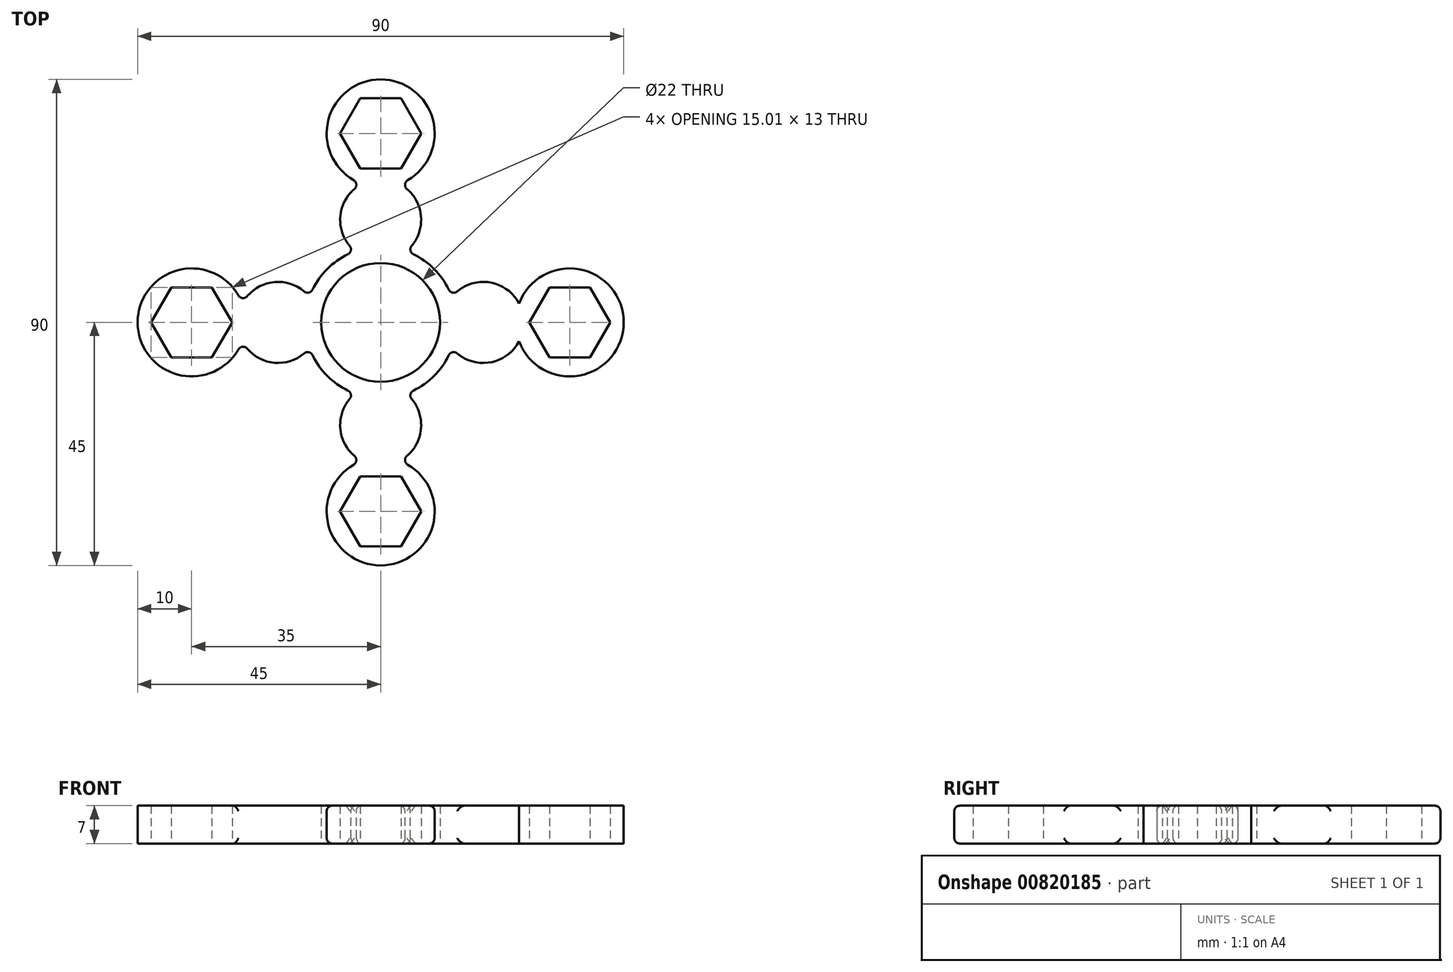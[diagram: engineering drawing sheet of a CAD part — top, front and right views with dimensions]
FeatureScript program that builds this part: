
annotation { "Feature Type Name" : "Feature", "Feature Type Description" : "" }
export const myFeature = defineFeature(function(context is Context, id is Id, definition is map)
    precondition{}
    {
        {
            var Q0;
            Q0=qCreatedBy(makeId("Top.planeOp"),FACE);
            var sketch = newSketch(context, id + "F0", { "sketchPlane" : qUnion([Q0])});
            skCircle(sketch, "E0", {"center": v(0, 0) * mm, "radius": 11 * mm});
            skCircle(sketch, "E1", {"center": v(0, 0) * mm, "radius": 14 * mm});
            skCircle(sketch, "E2", {"center": v(0, 19) * mm, "radius": 7.5 * mm});
            skCircle(sketch, "E3.MirrorC", {"center": v(0, -19) * mm, "radius": 7.5 * mm});
            skCircle(sketch, "E4", {"center": v(-19, 0) * mm, "radius": 7.5 * mm});
            skCircle(sketch, "E5.MirrorC", {"center": v(19, 0) * mm, "radius": 7.5 * mm});
            skCircle(sketch, "E6", {"center": v(-35, 0) * mm, "radius": 10 * mm});
            skCircle(sketch, "E7.MirrorC", {"center": v(35, 0) * mm, "radius": 10 * mm});
            skCircle(sketch, "E8", {"center": v(0, -35) * mm, "radius": 10 * mm});
            skCircle(sketch, "E9.MirrorC", {"center": v(0, 35) * mm, "radius": 10 * mm});
            skCircle(sketch, "E10.cCircle", {"center": v(0, 35) * mm, "radius": 6.5 * mm, "construction": true});
            skLineSegment(sketch, "E10.0", {"start": v(3.75, 28.5) * mm, "end": v(-3.75, 28.5) * mm});
            skLineSegment(sketch, "E10.1", {"start": v(-3.75, 28.5) * mm, "end": v(-7.5, 35) * mm});
            skLineSegment(sketch, "E10.2", {"start": v(-7.5, 35) * mm, "end": v(-3.75, 41.5) * mm});
            skLineSegment(sketch, "E10.3", {"start": v(-3.75, 41.5) * mm, "end": v(3.75, 41.5) * mm});
            skLineSegment(sketch, "E10.4", {"start": v(3.75, 41.5) * mm, "end": v(7.5, 35) * mm});
            skLineSegment(sketch, "E10.5", {"start": v(7.5, 35) * mm, "end": v(3.75, 28.5) * mm});
            skPoint(sketch, "E10.0.midPoint", {"position": v(0, 28.5) * mm});
            skLineSegment(sketch, "E11.MirrorCS", {"start": v(7.5, -35) * mm, "end": v(3.75, -28.5) * mm});
            skLineSegment(sketch, "E12.MirrorCS", {"start": v(3.75, -41.5) * mm, "end": v(7.5, -35) * mm});
            skLineSegment(sketch, "E13.MirrorCS", {"start": v(-3.75, -41.5) * mm, "end": v(3.75, -41.5) * mm});
            skLineSegment(sketch, "E14.MirrorCS", {"start": v(-7.5, -35) * mm, "end": v(-3.75, -41.5) * mm});
            skLineSegment(sketch, "E15.MirrorCS", {"start": v(-3.75, -28.5) * mm, "end": v(-7.5, -35) * mm});
            skLineSegment(sketch, "E16.MirrorCS", {"start": v(3.75, -28.5) * mm, "end": v(-3.75, -28.5) * mm});
            skCircle(sketch, "E17.cCircle", {"center": v(-35, 0) * mm, "radius": 6.5 * mm, "construction": true});
            skLineSegment(sketch, "E17.0", {"start": v(-38.75, 6.5) * mm, "end": v(-31.25, 6.5) * mm});
            skLineSegment(sketch, "E17.1", {"start": v(-31.25, 6.5) * mm, "end": v(-27.5, 0) * mm});
            skLineSegment(sketch, "E17.2", {"start": v(-27.5, 0) * mm, "end": v(-31.25, -6.5) * mm});
            skLineSegment(sketch, "E17.3", {"start": v(-31.25, -6.5) * mm, "end": v(-38.75, -6.5) * mm});
            skLineSegment(sketch, "E17.4", {"start": v(-38.75, -6.5) * mm, "end": v(-42.5, 0) * mm});
            skLineSegment(sketch, "E17.5", {"start": v(-42.5, 0) * mm, "end": v(-38.75, 6.5) * mm});
            skPoint(sketch, "E17.0.midPoint", {"position": v(-35, 6.5) * mm});
            skLineSegment(sketch, "E18.MirrorCS", {"start": v(27.5, 0) * mm, "end": v(31.25, -6.5) * mm});
            skLineSegment(sketch, "E19.MirrorCS", {"start": v(31.25, -6.5) * mm, "end": v(38.75, -6.5) * mm});
            skLineSegment(sketch, "E20.MirrorCS", {"start": v(38.75, -6.5) * mm, "end": v(42.5, 0) * mm});
            skLineSegment(sketch, "E21.MirrorCS", {"start": v(42.5, 0) * mm, "end": v(38.75, 6.5) * mm});
            skCircle(sketch, "E22.MirrorC", {"center": v(35, 0) * mm, "radius": 6.5 * mm, "construction": true});
            skLineSegment(sketch, "E23.MirrorCS", {"start": v(38.75, 6.5) * mm, "end": v(31.25, 6.5) * mm});
            skLineSegment(sketch, "E24.MirrorCS", {"start": v(31.25, 6.5) * mm, "end": v(27.5, 0) * mm});
            skSolve(sketch);
        }
        {
            var Q0;
            Q0 = qSketchRegion(id + "F0", true);
            extrude(context, id + "F1", {"entities" : qUnion([Q0]), "depth" : 7 * mm, "offsetDistance" : 25 * mm});
        }
        {
            var Q0;
            {var subQ0=sQuery(id+"F0.wireOp",EDGE,"E4");Q0=makeQuery(id+"F1.opExtrude","SWEPT_FACE",FACE,{"disambiguationData":[OSD([subQ0]),TDD([makeQuery(id+"F0.imprint","IMPRINT",EDGE,{"disambiguationData":[TD([[makeQuery(id+"F0.imprint","INTERSECT",VERTEX,{"disambiguationData":[OD(0.0)],"derivedFrom":[sQuery(id+"F0.wireOp",EDGE,"E1"),subQ0]}),-1.0]])],"derivedFrom":subQ0})])]});}
            var Q1;
            {var subQ0=sQuery(id+"F0.wireOp",EDGE,"E1");Q1=makeQuery(id+"F1.opExtrude","SWEPT_FACE",FACE,{"disambiguationData":[OSD([subQ0]),TDD([makeQuery(id+"F0.imprint","IMPRINT",EDGE,{"disambiguationData":[TD([[makeQuery(id+"F0.imprint","INTERSECT",VERTEX,{"disambiguationData":[OD(1.0)],"derivedFrom":[subQ0,sQuery(id+"F0.wireOp",EDGE,"E2")]}),-1.0]])],"derivedFrom":subQ0})])]});}
            var Q2;
            {var subQ0=sQuery(id+"F0.wireOp",EDGE,"E1");Q2=makeQuery(id+"F1.opExtrude","SWEPT_FACE",FACE,{"disambiguationData":[OSD([subQ0]),TDD([makeQuery(id+"F0.imprint","IMPRINT",EDGE,{"disambiguationData":[TD([[makeQuery(id+"F0.imprint","INTERSECT",VERTEX,{"disambiguationData":[OD(1.0)],"derivedFrom":[subQ0,sQuery(id+"F0.wireOp",EDGE,"E4")]}),-1.0]])],"derivedFrom":subQ0})])]});}
            var Q3;
            {var subQ0=sQuery(id+"F0.wireOp",EDGE,"E4");Q3=makeQuery(id+"F1.opExtrude","SWEPT_FACE",FACE,{"disambiguationData":[OSD([subQ0]),TDD([makeQuery(id+"F0.imprint","IMPRINT",EDGE,{"disambiguationData":[TD([[makeQuery(id+"F0.imprint","INTERSECT",VERTEX,{"disambiguationData":[OD(1.0)],"derivedFrom":[sQuery(id+"F0.wireOp",EDGE,"E1"),subQ0]}),1.0]])],"derivedFrom":subQ0})])]});}
            var Q4;
            {var subQ0=sQuery(id+"F0.wireOp",EDGE,"E1");Q4=makeQuery(id+"F1.opExtrude","SWEPT_FACE",FACE,{"disambiguationData":[OSD([subQ0]),TDD([makeQuery(id+"F0.imprint","IMPRINT",EDGE,{"disambiguationData":[TD([[makeQuery(id+"F0.imprint","INTERSECT",VERTEX,{"disambiguationData":[OD(1.0)],"derivedFrom":[subQ0,sQuery(id+"F0.wireOp",EDGE,"E3.MirrorC")]}),-1.0]])],"derivedFrom":subQ0})])]});}
            var Q5;
            {var subQ0=sQuery(id+"F0.wireOp",EDGE,"E5.MirrorC");Q5=makeQuery(id+"F1.opExtrude","SWEPT_FACE",FACE,{"disambiguationData":[OSD([subQ0]),TDD([makeQuery(id+"F0.imprint","IMPRINT",EDGE,{"disambiguationData":[TD([[makeQuery(id+"F0.imprint","INTERSECT",VERTEX,{"disambiguationData":[OD(1.0)],"derivedFrom":[sQuery(id+"F0.wireOp",EDGE,"E1"),subQ0]}),1.0]])],"derivedFrom":subQ0})])]});}
            var Q6;
            {var subQ0=sQuery(id+"F0.wireOp",EDGE,"E5.MirrorC");Q6=makeQuery(id+"F1.opExtrude","SWEPT_FACE",FACE,{"disambiguationData":[OSD([subQ0]),TDD([makeQuery(id+"F0.imprint","IMPRINT",EDGE,{"disambiguationData":[TD([[makeQuery(id+"F0.imprint","INTERSECT",VERTEX,{"disambiguationData":[OD(0.0)],"derivedFrom":[sQuery(id+"F0.wireOp",EDGE,"E1"),subQ0]}),-1.0]])],"derivedFrom":subQ0})])]});}
            var Q7;
            {var subQ0=sQuery(id+"F0.wireOp",EDGE,"E1");Q7=makeQuery(id+"F1.opExtrude","SWEPT_FACE",FACE,{"disambiguationData":[OSD([subQ0]),TDD([makeQuery(id+"F0.imprint","IMPRINT",EDGE,{"disambiguationData":[TD([[makeQuery(id+"F0.imprint","INTERSECT",VERTEX,{"disambiguationData":[OD(0.0)],"derivedFrom":[subQ0,sQuery(id+"F0.wireOp",EDGE,"E2")]}),1.0]])],"derivedFrom":subQ0})])]});}
            var Q8;
            Q8=makeQuery(id+"F1.opExtrude","SWEPT_FACE",FACE,{"disambiguationData":[OSD([sQuery(id+"F0.wireOp",EDGE,"E8")])]});
            var Q9;
            Q9=makeQuery(id+"F1.opExtrude","SWEPT_FACE",FACE,{"disambiguationData":[OSD([sQuery(id+"F0.wireOp",EDGE,"E9.MirrorC")])]});
            fillet(context, id + "F2", {"entities" : qUnion([Q0, Q1, Q2, Q3, Q4, Q5, Q6, Q7, Q8, Q9]), "radius" : 1 * mm, "tangentPropagation" : true, "allowEdgeOverflow" : false});
        }
    });
